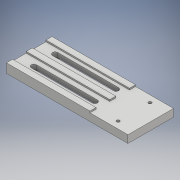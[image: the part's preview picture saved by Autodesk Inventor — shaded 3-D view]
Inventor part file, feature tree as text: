
AUTODESK INVENTOR PART (.ipt)
format: ipt  version: 2018 (Build 220112000, 112)  size: 158,720 bytes
history: native  units: mm
features: extrude x2, sketch x2, chamfer x1
ambient origin geometry x8: Origin, YZ Plane, XZ Plane, XY Plane, X Axis, Y Axis, Z Axis, Center Point
bodies: Solid1 (feature_tree)
feature tree (5):
  extrude  "Extrusion1"  Depth=11.0mm
  extrude  "Extrusion2"  Depth=1.0mm
  chamfer  "Chamfer1"  Distance=4.5mm
  sketch  "Sketch1"  dims[d0=21.0mm d1=11.0mm]
  sketch  "Sketch2"  dims[d2=30.0mm d3=2.0mm d4=4.5mm d5=80.0mm d6=3.5mm d7=3.5mm d8=10.0mm d10=10.0mm d11=8.0mm d12=8.0mm d13=18.875mm d14=18.875mm d15=5.0mm d16=0.0mm d17=4.0mm d18=4.0mm d19=4.0mm d20=55.0mm d21=1.0mm d22=0.0mm d23=2.0mm d24=2.0mm d25=45.0deg]
